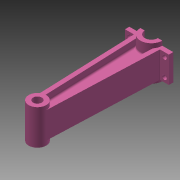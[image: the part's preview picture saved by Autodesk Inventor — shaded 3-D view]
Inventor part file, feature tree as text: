
AUTODESK INVENTOR PART (.ipt)
format: ipt  version: 2015 (Build 190159000, 159)  size: 241,664 bytes
history: native  units: mm
features: extrude x4, sketch x4, pattern_linear x2, fillet x2
ambient origin geometry x8: Origin, YZ Plane, XZ Plane, XY Plane, X Axis, Y Axis, Z Axis, Center Point
bodies: 实体1 (feature_tree)
feature tree (12):
  extrude  "拉伸1"  Depth=15.0mm
  extrude  "拉伸2"  Depth=10.0mm
  pattern_linear  "矩形阵列1"  Spacing1=5.0mm  [1 undecoded]
  extrude  "拉伸3"  Depth=50.0mm
  pattern_linear  "矩形阵列2"  Count1=4 Spacing1=0.0mm
  extrude  "拉伸4"  Depth=0.25mm
  fillet  "圆角1"  Radius=10.0mm
  fillet  "圆角2"  Radius=5.0mm
  sketch  "草图1"  dims[d0=30.0mm d1=15.0mm]
  sketch  "草图2"  dims[d2=20.0mm d3=10.0mm]
  sketch  "草图3"  dims[d4=6.036447mm]
  sketch  "草图4"  dims[d5=129.8mm d6=5.0mm d7=50.0mm d8=40.0mm d9=0.0mm d10=12.5mm d11=10.0mm d12=5.0mm d13=5.0mm d14=13.0mm d15=0.0mm d16=20.0mm d18=27.0mm d19=12.5mm d20=5.0mm d21=0.0mm d22=20.0mm d24=35.0mm d25=5.0mm d26=5.0mm d27=5.0mm d28=5.0mm d29=5.0mm d30=5.0mm d31=5.0mm d32=5.0mm d33=5.0mm d34=5.0mm d35=5.0mm d36=5.0mm d37=5.0mm d38=0.0mm d39=2.0mm d40=0.25mm]
note: 1 required parameter value undecoded (feature->parameter linkage not recoverable at this tier; creation-order binding heuristic only, values carry confidence <= 0.55)
